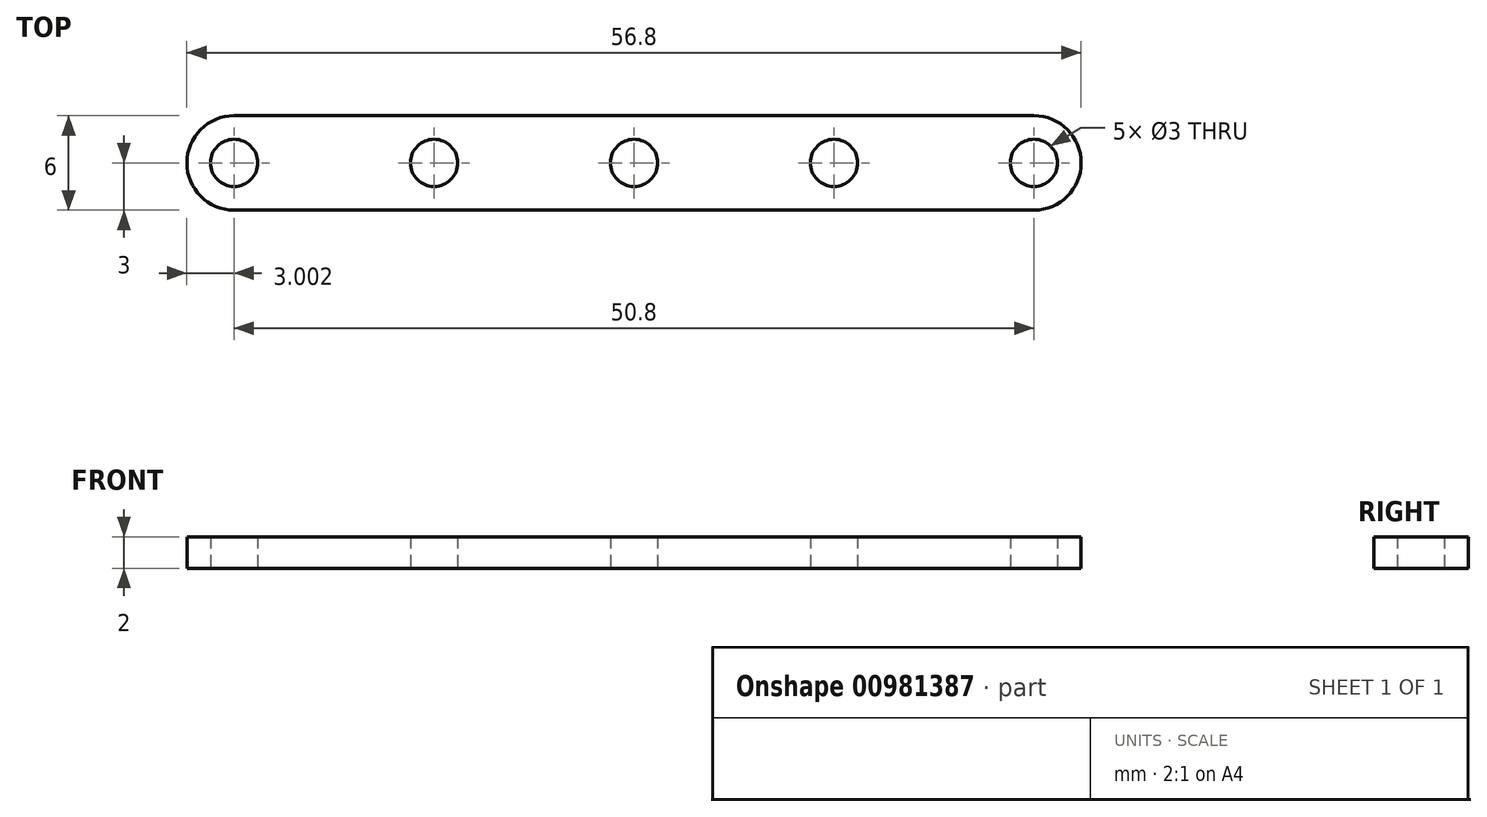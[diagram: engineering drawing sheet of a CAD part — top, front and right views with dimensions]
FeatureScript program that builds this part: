
annotation { "Feature Type Name" : "Feature", "Feature Type Description" : "" }
export const myFeature = defineFeature(function(context is Context, id is Id, definition is map)
    precondition{}
    {
        {
            var Q0;
            Q0=qCreatedBy(makeId("Top.planeOp"),FACE);
            var sketch = newSketch(context, id + "F0", { "sketchPlane" : qUnion([Q0])});
            skCircle(sketch, "E0", {"center": v(-44.77, 0) * mm, "radius": 1.5 * mm});
            skCircle(sketch, "E1.1.0.0", {"center": v(-32.07, 0) * mm, "radius": 1.5 * mm});
            skCircle(sketch, "E1.2.0.0", {"center": v(-19.37, 0) * mm, "radius": 1.5 * mm});
            skCircle(sketch, "E1.3.0.0", {"center": v(-6.67, 0) * mm, "radius": 1.5 * mm});
            skCircle(sketch, "E1.4.0.0", {"center": v(6.03, 0) * mm, "radius": 1.5 * mm});
            skLineSegment(sketch, "E1.direction1", {"start": v(-44.77, 0) * mm, "end": v(-32.07, 0) * mm, "construction": true});
            skLineSegment(sketch, "E2", {"start": v(-44.77, 3) * mm, "end": v(6.03, 3) * mm});
            skLineSegment(sketch, "E3", {"start": v(6.03, -3) * mm, "end": v(-44.77, -3) * mm});
            skArc(sketch, "E4", {"start": v(-44.77, -3) * mm, "mid": v(-47.77, 0) * mm, "end": v(-44.77, 3) * mm});
            skArc(sketch, "E5", {"start": v(6.03, 3) * mm, "mid": v(9.03, 0) * mm, "end": v(6.03, -3) * mm});
            skSolve(sketch);
        }
        {
            var Q0;
            Q0=makeQuery(id+"F0.imprint","IMPRINT",FACE,{"disambiguationData":[TD([[makeQuery(id+"F0.imprint","IMPRINT",EDGE,{"derivedFrom":sQuery(id+"F0.wireOp",EDGE,"E0")}),-1.0]])]});
            extrude(context, id + "F1", {"entities" : qUnion([Q0]), "depth" : 2 * mm, "offsetDistance" : 25 * mm});
        }
    });
